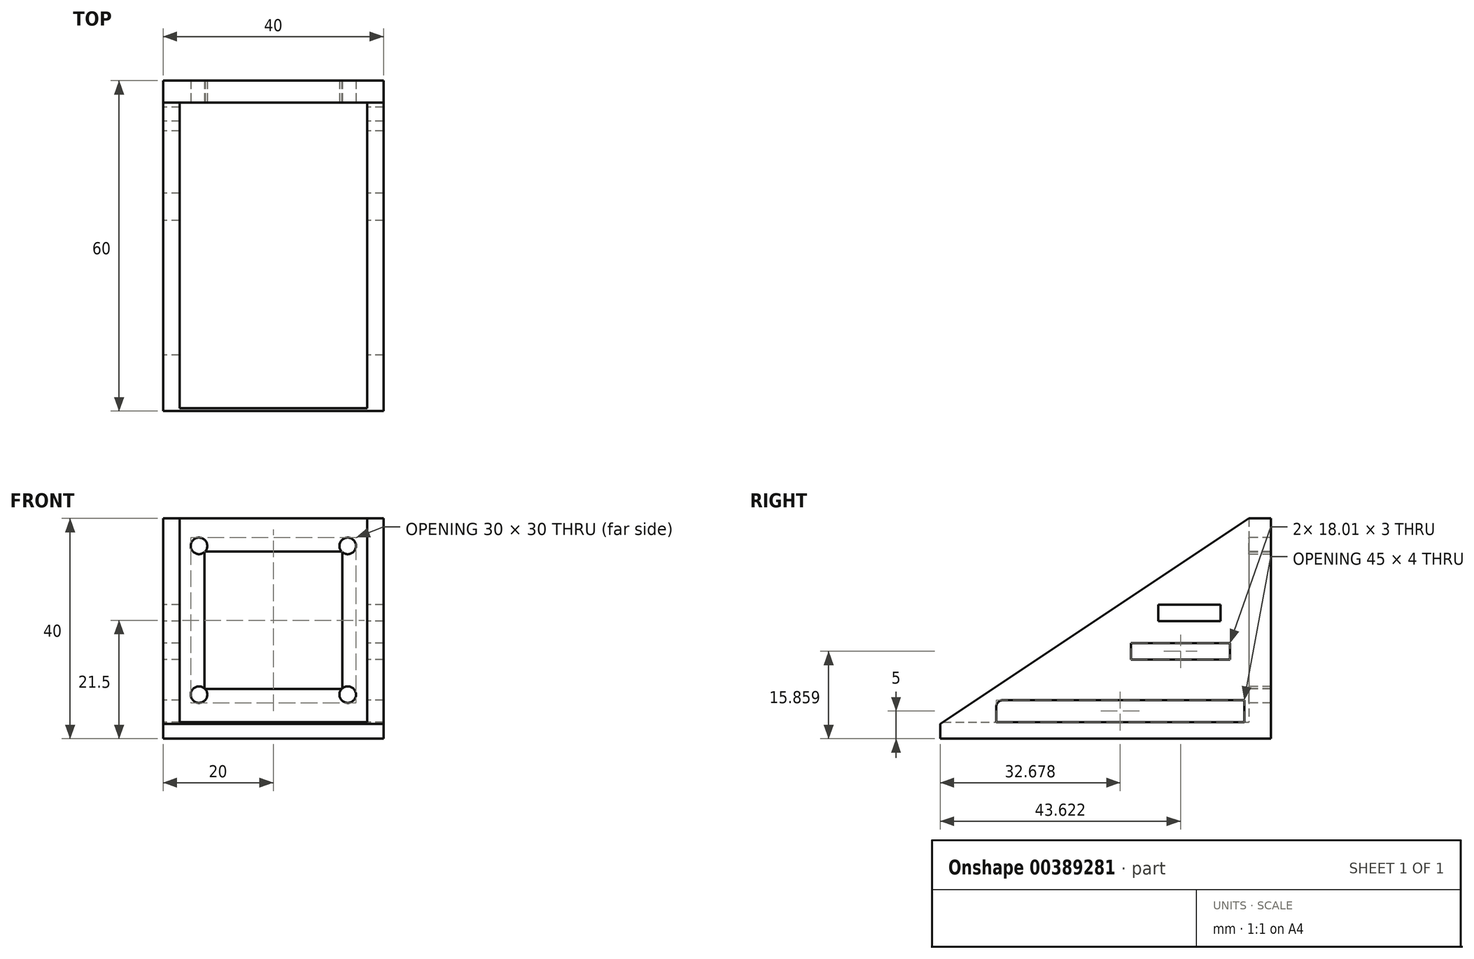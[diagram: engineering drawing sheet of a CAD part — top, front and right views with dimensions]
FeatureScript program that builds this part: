
annotation { "Feature Type Name" : "Feature", "Feature Type Description" : "" }
export const myFeature = defineFeature(function(context is Context, id is Id, definition is map)
    precondition{}
    {
        {
            var Q0;
            Q0=qCreatedBy(makeId("Top.planeOp"),FACE);
            var sketch = newSketch(context, id + "F0", { "sketchPlane" : qUnion([Q0])});
            skLineSegment(sketch, "E0.bottom", {"start": v(0, 0) * mm, "end": v(-40, 0) * mm});
            skLineSegment(sketch, "E0.top", {"start": v(0, 60) * mm, "end": v(-40, 60) * mm});
            skLineSegment(sketch, "E0.left", {"start": v(0, 0) * mm, "end": v(0, 60) * mm});
            skLineSegment(sketch, "E0.right", {"start": v(-40, 0) * mm, "end": v(-40, 60) * mm});
            skLineSegment(sketch, "E1", {"start": v(-40, 56) * mm, "end": v(0, 56) * mm});
            skSolve(sketch);
        }
        {
            var Q0;
            Q0=makeQuery(id+"F0.imprint","IMPRINT",FACE,{"disambiguationData":[TD([[makeQuery(id+"F0.imprint","IMPRINT",EDGE,{"derivedFrom":sQuery(id+"F0.wireOp",EDGE,"E0.bottom")}),-1.0]])]});
            extrude(context, id + "F1", {"entities" : qUnion([Q0]), "depth" : 3 * mm, "offsetDistance" : 25 * mm});
        }
        {
            var Q0;
            {var subQ0=sQuery(id+"F0.wireOp",EDGE,"E0.top");Q0=makeQuery(id+"F0.imprint","IMPRINT",FACE,{"disambiguationData":[TD([[makeQuery(id+"F0.imprint","IMPRINT",EDGE,{"derivedFrom":subQ0}),1.0]])]});}
            extrude(context, id + "F2", {"entities" : qUnion([Q0]), "operationType" : NewBodyOperationType.ADD, "depth" : 40 * mm, "offsetDistance" : 25 * mm});
        }
        {
            var Q0;
            Q0=makeQuery(id+"F2.opExtrude","SWEPT_FACE",FACE,{"disambiguationData":[OSD([sQuery(id+"F0.wireOp",EDGE,"E1")])]});
            var sketch = newSketch(context, id + "F3", { "sketchPlane" : qUnion([Q0])});
            skLineSegment(sketch, "E2.bottom", {"start": v(-40, 40) * mm, "end": v(-37, 40) * mm});
            skLineSegment(sketch, "E2.top", {"start": v(-40, 3) * mm, "end": v(-37, 3) * mm});
            skLineSegment(sketch, "E2.left", {"start": v(-40, 40) * mm, "end": v(-40, 3) * mm});
            skLineSegment(sketch, "E2.right", {"start": v(-37, 40) * mm, "end": v(-37, 3) * mm});
            skLineSegment(sketch, "E3.bottom", {"start": v(-3, 40) * mm, "end": v(0, 40) * mm});
            skLineSegment(sketch, "E3.top", {"start": v(-3, 3) * mm, "end": v(0, 3) * mm});
            skLineSegment(sketch, "E3.left", {"start": v(-3, 40) * mm, "end": v(-3, 3) * mm});
            skLineSegment(sketch, "E3.right", {"start": v(0, 40) * mm, "end": v(0, 3) * mm});
            skSolve(sketch);
        }
        {
            var Q0;
            Q0 = qSketchRegion(id + "F3", true);
            extrude(context, id + "F4", {"entities" : qUnion([Q0]), "operationType" : NewBodyOperationType.ADD, "depth" : 56 * mm, "offsetDistance" : 25 * mm});
        }
        {
            var Q0;
            {var subQ0=sQuery(id+"F0.wireOp",EDGE,"E0.right");Q0=makeQuery(id+"F4.boolean.opBoolean","MERGE",FACE,{"derivedFrom":[makeQuery(id+"F2.boolean.opBoolean","MERGE",FACE,{"derivedFrom":[makeQuery(id+"F1.opExtrude","SWEPT_FACE",FACE,{"disambiguationData":[OSD([subQ0])]}),makeQuery(id+"F2.opExtrude","SWEPT_FACE",FACE,{"disambiguationData":[OSD([subQ0])]})]}),makeQuery(id+"F4.opExtrude","SWEPT_FACE",FACE,{"disambiguationData":[OSD([sQuery(id+"F3.wireOp",EDGE,"E2.left")])]})]});}
            var sketch = newSketch(context, id + "F5", { "sketchPlane" : qUnion([Q0])});
            skLineSegment(sketch, "E4", {"start": v(-56, 40) * mm, "end": v(0, 2.66) * mm});
            skSolve(sketch);
        }
        {
            var Q0;
            Q0 = qSketchRegion(id + "F5", true);
            var Q1;
            {var subQ0=sQuery(id+"F5.wireOp",EDGE,"E4");Q1=makeQuery(id+"F5.imprint","IMPRINT",FACE,{"disambiguationData":[TD([[makeQuery(id+"F5.imprint","IMPRINT",EDGE,{"derivedFrom":subQ0}),1.0]])]});}
            extrude(context, id + "F6", {"entities" : qUnion([Q0, Q1]), "operationType" : NewBodyOperationType.REMOVE, "endBound" : BoundingType.THROUGH_ALL, "oppositeDirection" : true, "depth" : 25 * mm, "offsetDistance" : 25 * mm});
        }
        {
            var Q0;
            Q0=makeQuery(id+"F2.opExtrude","SWEPT_FACE",FACE,{"disambiguationData":[OSD([sQuery(id+"F0.wireOp",EDGE,"E1")])]});
            var sketch = newSketch(context, id + "F7", { "sketchPlane" : qUnion([Q0])});
            skLineSegment(sketch, "E5.bottom", {"start": v(-32.5, 34) * mm, "end": v(-7.5, 34) * mm});
            skLineSegment(sketch, "E5.top", {"start": v(-32.5, 9) * mm, "end": v(-7.5, 9) * mm});
            skLineSegment(sketch, "E5.left", {"start": v(-32.5, 34) * mm, "end": v(-32.5, 9) * mm});
            skLineSegment(sketch, "E5.right", {"start": v(-7.5, 34) * mm, "end": v(-7.5, 9) * mm});
            skLineSegment(sketch, "E6", {"start": v(-20, 9) * mm, "end": v(-20, 34) * mm, "construction": true});
            skLineSegment(sketch, "E7", {"start": v(-32.5, 21.5) * mm, "end": v(-7.5, 21.5) * mm, "construction": true});
            skCircle(sketch, "E8", {"center": v(-33.5, 35) * mm, "radius": 1.5 * mm});
            skCircle(sketch, "E9.1.0.0", {"center": v(-6.5, 35) * mm, "radius": 1.5 * mm});
            skLineSegment(sketch, "E9.direction1", {"start": v(-33.5, 35) * mm, "end": v(-6.5, 35) * mm, "construction": true});
            skCircle(sketch, "E10", {"center": v(-33.5, 8) * mm, "radius": 1.5 * mm});
            skCircle(sketch, "E11.1.0.0", {"center": v(-6.5, 8) * mm, "radius": 1.5 * mm});
            skLineSegment(sketch, "E11.direction1", {"start": v(-33.5, 8) * mm, "end": v(-6.5, 8) * mm, "construction": true});
            skSolve(sketch);
        }
        {
            var Q0;
            Q0=makeQuery(id+"F7.imprint","IMPRINT",FACE,{"disambiguationData":[TD([[makeQuery(id+"F7.imprint","IMPRINT",EDGE,{"derivedFrom":sQuery(id+"F7.wireOp",EDGE,"E5.bottom")}),-1.0]])]});
            var Q1;
            Q1=makeQuery(id+"F7.imprint","IMPRINT",FACE,{"disambiguationData":[TD([[makeQuery(id+"F7.imprint","IMPRINT",EDGE,{"derivedFrom":sQuery(id+"F7.wireOp",EDGE,"E8")}),1.0]])]});
            var Q2;
            {var subQ5=sQuery(id+"F7.wireOp",EDGE,"E8");var subQ13=sQuery(id+"F7.wireOp",EDGE,"E5.bottom");var subQ14=makeQuery(id+"F7.imprint","INTERSECT",VERTEX,{"derivedFrom":[subQ13,subQ5]});Q2=makeQuery(id+"F7.imprint","IMPRINT",FACE,{"disambiguationData":[TD([[makeQuery(id+"F7.imprint","IMPRINT",EDGE,{"disambiguationData":[TD([[subQ14,-1.0]])],"derivedFrom":subQ13}),-1.0]])]});}
            var Q3;
            {var subQ0=sQuery(id+"F7.wireOp",EDGE,"E5.left");var subQ1=sQuery(id+"F7.wireOp",EDGE,"E5.top");var subQ2=makeQuery(id+"F7.imprint","INTERSECT",VERTEX,{"derivedFrom":[subQ1,subQ0]});Q3=makeQuery(id+"F7.imprint","IMPRINT",FACE,{"disambiguationData":[TD([[makeQuery(id+"F7.imprint","IMPRINT",EDGE,{"disambiguationData":[TD([[subQ2,-1.0]])],"derivedFrom":subQ1}),-1.0]])]});}
            var Q4;
            {var subQ0=sQuery(id+"F7.wireOp",EDGE,"E5.right");var subQ1=sQuery(id+"F7.wireOp",EDGE,"E5.bottom");var subQ2=makeQuery(id+"F7.imprint","INTERSECT",VERTEX,{"derivedFrom":[subQ1,subQ0]});Q4=makeQuery(id+"F7.imprint","IMPRINT",FACE,{"disambiguationData":[TD([[makeQuery(id+"F7.imprint","IMPRINT",EDGE,{"disambiguationData":[TD([[subQ2,1.0]])],"derivedFrom":subQ1}),1.0]])]});}
            var Q5;
            {var subQ0=sQuery(id+"F7.wireOp",EDGE,"E5.right");var subQ1=sQuery(id+"F7.wireOp",EDGE,"E5.top");var subQ2=makeQuery(id+"F7.imprint","INTERSECT",VERTEX,{"derivedFrom":[subQ1,subQ0]});Q5=makeQuery(id+"F7.imprint","IMPRINT",FACE,{"disambiguationData":[TD([[makeQuery(id+"F7.imprint","IMPRINT",EDGE,{"disambiguationData":[TD([[subQ2,1.0]])],"derivedFrom":subQ1}),-1.0]])]});}
            extrude(context, id + "F8", {"entities" : qUnion([Q0, Q1, Q2, Q3, Q4, Q5]), "operationType" : NewBodyOperationType.REMOVE, "endBound" : BoundingType.THROUGH_ALL, "oppositeDirection" : true, "depth" : 25 * mm, "offsetDistance" : 25 * mm});
        }
        {
            var Q0;
            {var subQ4=sQuery(id+"F5.wireOp",EDGE,"E4");Q0=makeQuery(id+"F5.imprint","IMPRINT",FACE,{"disambiguationData":[TD([[makeQuery(id+"F5.imprint","IMPRINT",EDGE,{"derivedFrom":subQ4}),-1.0]])]});}
            var sketch = newSketch(context, id + "F9", { "sketchPlane" : qUnion([Q0])});
            skLineSegment(sketch, "E12.bottom", {"start": v(-55.18, 3) * mm, "end": v(-10.18, 3) * mm});
            skLineSegment(sketch, "E12.top", {"start": v(-55.18, 7) * mm, "end": v(-11.43, 7) * mm});
            skLineSegment(sketch, "E12.left", {"start": v(-55.18, 3) * mm, "end": v(-55.18, 7) * mm});
            skLineSegment(sketch, "E12.right", {"start": v(-10.18, 3) * mm, "end": v(-10.18, 5.75) * mm});
            skPoint(sketch, "E13.visualSharp", {"position": v(-10.18, 7) * mm});
            skArc(sketch, "E13.filletArc", {"start": v(-10.18, 5.75) * mm, "mid": v(-10.55, 6.63) * mm, "end": v(-11.43, 7) * mm});
            skLineSegment(sketch, "E14.bottom", {"start": v(-50.9, 24.35) * mm, "end": v(-39.6, 24.35) * mm});
            skLineSegment(sketch, "E14.top", {"start": v(-50.9, 21.35) * mm, "end": v(-39.6, 21.35) * mm});
            skLineSegment(sketch, "E14.left", {"start": v(-50.9, 24.35) * mm, "end": v(-50.9, 21.35) * mm});
            skLineSegment(sketch, "E14.right", {"start": v(-39.6, 24.35) * mm, "end": v(-39.6, 21.35) * mm});
            skLineSegment(sketch, "E15.bottom", {"start": v(-52.63, 17.36) * mm, "end": v(-34.62, 17.36) * mm});
            skLineSegment(sketch, "E15.top", {"start": v(-52.63, 14.36) * mm, "end": v(-34.62, 14.36) * mm});
            skLineSegment(sketch, "E15.left", {"start": v(-52.63, 17.36) * mm, "end": v(-52.63, 14.36) * mm});
            skLineSegment(sketch, "E15.right", {"start": v(-34.62, 17.36) * mm, "end": v(-34.62, 14.36) * mm});
            skSolve(sketch);
        }
        {
            var Q0;
            Q0 = qSketchRegion(id + "F9", true);
            extrude(context, id + "F10", {"entities" : qUnion([Q0]), "operationType" : NewBodyOperationType.REMOVE, "endBound" : BoundingType.THROUGH_ALL, "oppositeDirection" : true, "depth" : 25 * mm, "offsetDistance" : 25 * mm});
        }
    });
